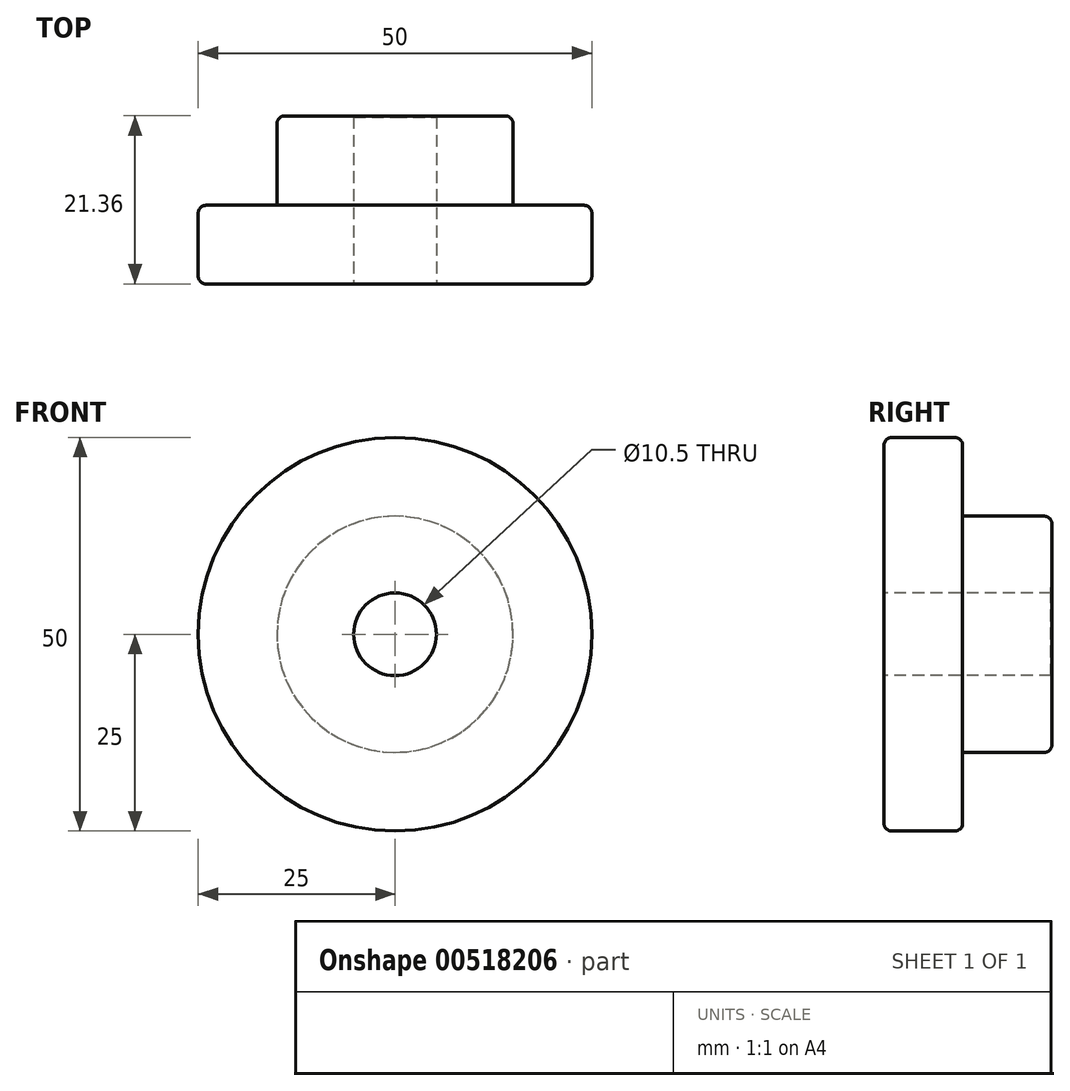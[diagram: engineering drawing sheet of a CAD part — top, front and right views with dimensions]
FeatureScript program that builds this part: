
annotation { "Feature Type Name" : "Feature", "Feature Type Description" : "" }
export const myFeature = defineFeature(function(context is Context, id is Id, definition is map)
    precondition{}
    {
        {
            var Q0;
            Q0=qCreatedBy(makeId("Right.planeOp"),FACE);
            var sketch = newSketch(context, id + "F0", { "sketchPlane" : qUnion([Q0])});
            skLineSegment(sketch, "E0", {"start": v(0, 0) * mm, "end": v(0, 25) * mm});
            skLineSegment(sketch, "E1", {"start": v(0, 25) * mm, "end": v(10, 25) * mm});
            skLineSegment(sketch, "E2", {"start": v(10, 25) * mm, "end": v(10, 15) * mm});
            skLineSegment(sketch, "E3", {"start": v(10, 15) * mm, "end": v(21.37, 15) * mm});
            skLineSegment(sketch, "E4", {"start": v(21.37, 15) * mm, "end": v(21.23, 5.25) * mm});
            skLineSegment(sketch, "E5", {"start": v(21.23, 5.25) * mm, "end": v(-0.77, 5.25) * mm});
            skLineSegment(sketch, "E6", {"start": v(0, 0) * mm, "end": v(31.37, 0) * mm, "construction": true});
            skSolve(sketch);
        }
        {
            var Q0;
            Q0 = qSketchRegion(id + "F0", true);
            var Q1;
            Q1=sQuery(id+"F0.wireOp",EDGE,"E6");
            revolve(context, id + "F1", {"entities" : qUnion([Q0]), "axis" : qUnion([Q1]), "revolveType" : RevolveType.FULL});
        }
        {
            var Q0;
            Q0=makeQuery(id+"F1.opRevolve","SWEPT_EDGE",EDGE,{"disambiguationData":[OSD([sQuery(id+"F0.wireOp",EDGE,"E0"),sQuery(id+"F0.wireOp",EDGE,"E1")])]});
            var Q1;
            Q1=makeQuery(id+"F1.opRevolve","SWEPT_EDGE",EDGE,{"disambiguationData":[OSD([sQuery(id+"F0.wireOp",EDGE,"E1"),sQuery(id+"F0.wireOp",EDGE,"E2")])]});
            var Q2;
            Q2=makeQuery(id+"F1.opRevolve","SWEPT_EDGE",EDGE,{"disambiguationData":[OSD([sQuery(id+"F0.wireOp",EDGE,"E3"),sQuery(id+"F0.wireOp",EDGE,"E4")])]});
            fillet(context, id + "F2", {"entities" : qUnion([Q0, Q1, Q2]), "radius" : 1 * mm, "tangentPropagation" : true, "allowEdgeOverflow" : false});
        }
    });
